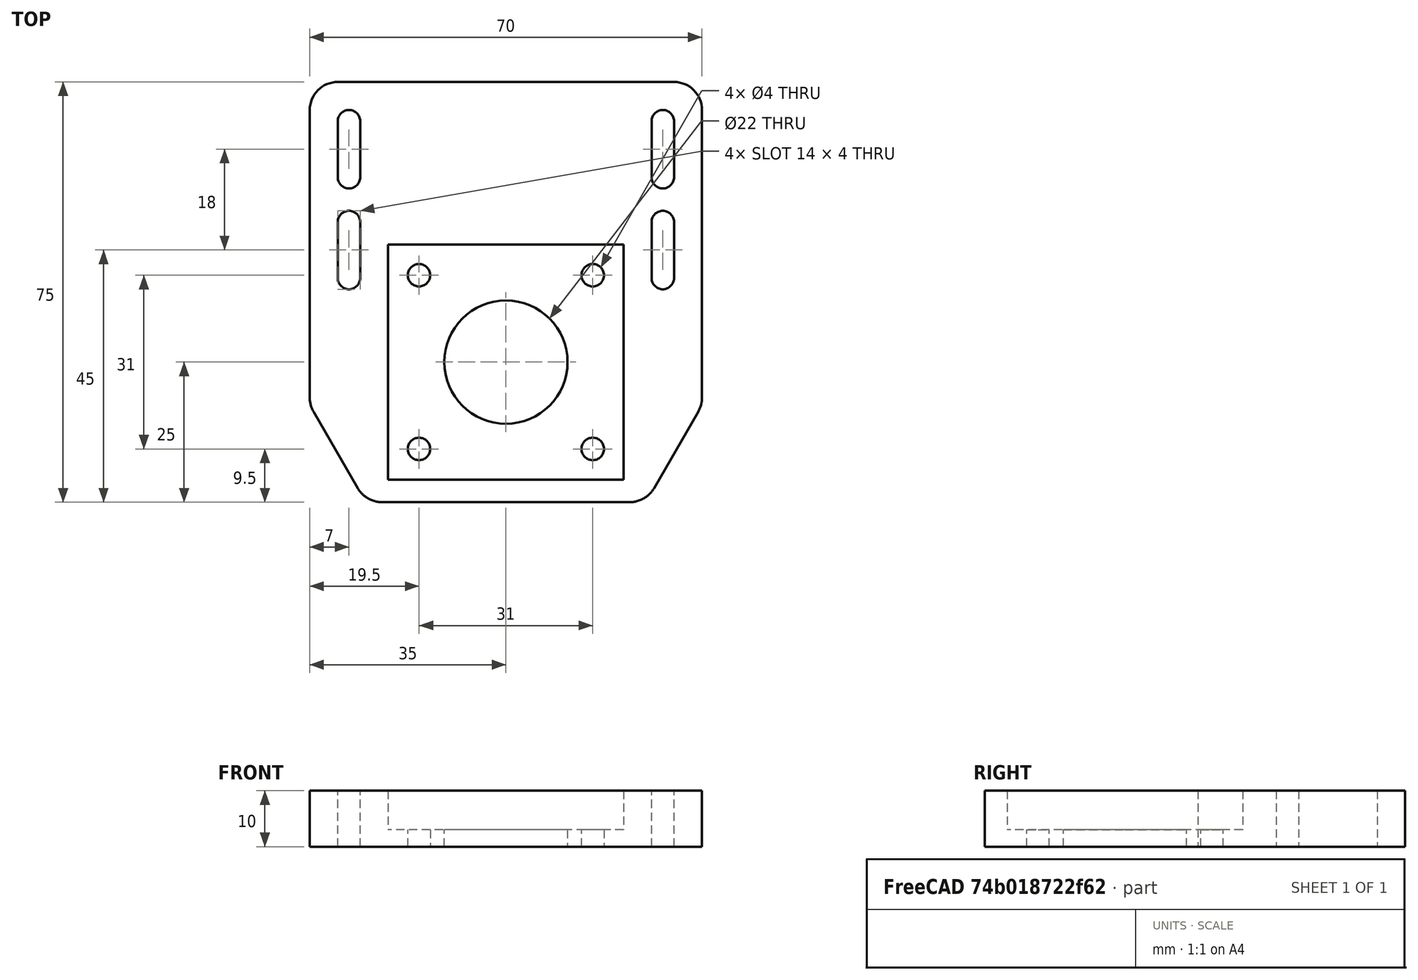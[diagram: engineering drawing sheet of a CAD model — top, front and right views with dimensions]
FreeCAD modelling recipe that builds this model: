
FCSTD DOCUMENT  (FreeCAD 2020.12.13R23076 +3015 (Git))
Label: krokowiec-dol
License: All rights reserved
objects: Sketcher::SketchObject×7, PartDesign::Pocket×4, PartDesign::Pad×2, PartDesign::LinearPattern×2, TechDraw::DrawProjGroupItem×2, TechDraw::DrawViewDimension×2, TechDraw::DrawSVGTemplate×1, PartDesign::MultiTransform×1, PartDesign::Fillet×1, PartDesign::Body×1, TechDraw::DrawProjGroup×1, TechDraw::DrawPage×1
note: 35 computed .brp shape members not serialized (recipe doc carries the construction recipe); baked Part::Feature solids carry a one-line shape summary decoded from their .brp

FEATURE [Sketcher::SketchObject] Sketch
  MapMode = 5
  Support = -> [XY_Plane]
  sketch-geometry (5):
    g0: LineSegment StartX=25 StartY=25 StartZ=0 EndX=-25 EndY=25 EndZ=0
    g1: LineSegment StartX=-25 StartY=-25 StartZ=0 EndX=25 EndY=-25 EndZ=0
    g2: Circle [constr] CenterX=0 CenterY=0 CenterZ=0 NormalX=0 NormalY=0 NormalZ=1 AngleXU=0 Radius=35.3553
    g3: LineSegment StartX=-25 StartY=25 StartZ=0 EndX=-25 EndY=-25 EndZ=0
    g4: LineSegment StartX=25 StartY=25 StartZ=0 EndX=25 EndY=-25 EndZ=0
  constraints (14):
    c: Equal(g0,g1)
    c: PointOnObject(g0,g2)
    c: PointOnObject(g1,g2)
    c: PointOnObject(g1,g2)
    c: PointOnObject(g0,g2)
    c: Coincident(g2,g-1)
    c: Horizontal(g0)
    c: DistanceX(g0,g0) = 50
    c: DistanceY(g1,g0) = 50
    c: Horizontal(g1)
    c: Coincident(g0,g3)
    c: Coincident(g3,g1)
    c: Coincident(g0,g4)
    c: Coincident(g4,g1)
FEATURE [PartDesign::Pad] Pad
  ClaimChildren = false
  Direction = (1,1,1)
  Fit = 0
  FitJoin = 0
  InnerFit = 0
  InnerFitJoin = 0
  InnerTaperAngle = 0
  InnerTaperAngleRev = 0
  Length = 10
  Length2 = 100
  NewSolid = false
  Profile = -> Sketch
  Suppress = false
  Type = 0
FEATURE [Sketcher::SketchObject] Sketch001
  MapMode = 5
  Placement = pos=(0,0,10) rot=(0,0,1;0rad)
  Support = -> [Pad]
  sketch-geometry (5):
    g0: LineSegment StartX=21 StartY=21 StartZ=0 EndX=-21 EndY=21 EndZ=0
    g1: LineSegment StartX=-21 StartY=21 StartZ=0 EndX=-21 EndY=-21 EndZ=0
    g2: LineSegment StartX=-21 StartY=-21 StartZ=0 EndX=21 EndY=-21 EndZ=0
    g3: LineSegment StartX=21 StartY=-21 StartZ=0 EndX=21 EndY=21 EndZ=0
    g4: Circle [constr] CenterX=0 CenterY=0 CenterZ=0 NormalX=0 NormalY=0 NormalZ=1 AngleXU=0 Radius=29.6985
  constraints (14):
    c: Coincident(g0,g1)
    c: Coincident(g1,g2)
    c: Coincident(g2,g3)
    c: Coincident(g3,g0)
    c: Equal(g0,g1)
    c: Equal(g0,g2)
    c: Equal(g0,g3)
    c: PointOnObject(g0,g4)
    c: PointOnObject(g1,g4)
    c: PointOnObject(g2,g4)
    c: PointOnObject(g3,g4)
    c: Coincident(g4,g-1)
    c: DistanceX(g0,g0) = 42
    c: Horizontal(g0)
FEATURE [PartDesign::Pocket] Pocket
  BaseFeature = -> Pad
  ClaimChildren = false
  Fit = 0
  FitJoin = 0
  InnerFit = 0
  InnerFitJoin = 0
  InnerTaperAngle = 0
  InnerTaperAngleRev = 0
  Length = 7
  Length2 = 100
  NewSolid = false
  Profile = -> Sketch001
  Suppress = false
  Type = 0
FEATURE [Sketcher::SketchObject] Sketch002
  MapMode = 5
  Placement = pos=(0,0,3) rot=(0,0,1;0rad)
  Support = -> [Pocket]
  sketch-geometry (1):
    g0: Circle CenterX=0 CenterY=0 CenterZ=0 NormalX=0 NormalY=0 NormalZ=1 AngleXU=0 Radius=11
  constraints (2):
    c: Coincident(g0,g-1)
    c: Diameter(g0) = 22
FEATURE [PartDesign::Pocket] Pocket001
  BaseFeature = -> Pocket
  ClaimChildren = false
  Fit = 0
  FitJoin = 0
  InnerFit = 0
  InnerFitJoin = 0
  InnerTaperAngle = 0
  InnerTaperAngleRev = 0
  Length = 5
  Length2 = 100
  NewSolid = false
  Profile = -> Sketch002
  Suppress = false
  Type = 1
FEATURE [Sketcher::SketchObject] Sketch005
  MapMode = 5
  Placement = pos=(0,0,5) rot=(0,0,1;0rad)
  sketch-geometry (4):
    g0: Circle CenterX=-15.5 CenterY=15.5 CenterZ=0 NormalX=0 NormalY=0 NormalZ=1 AngleXU=0 Radius=2
    g1: Circle CenterX=15.5 CenterY=15.5 CenterZ=0 NormalX=0 NormalY=0 NormalZ=1 AngleXU=0 Radius=2
    g2: Circle CenterX=15.5 CenterY=-15.5 CenterZ=0 NormalX=0 NormalY=0 NormalZ=1 AngleXU=0 Radius=2
    g3: Circle CenterX=-15.5 CenterY=-15.5 CenterZ=0 NormalX=0 NormalY=0 NormalZ=1 AngleXU=0 Radius=2
  constraints (9):
    c: Symmetric(g3,g0,g-1)
    c: Symmetric(g0,g1,g-2)
    c: Symmetric(g2,g1,g-1)
    c: Equal(g3,g2)
    c: Equal(g2,g1)
    c: Equal(g1,g0)
    c: DistanceX(g0,g1) = 31
    c: DistanceY(g2,g1) = 31
    c: Diameter(g1) = 4
FEATURE [PartDesign::Pocket] Pocket004
  BaseFeature = -> Pocket001
  ClaimChildren = false
  Fit = 0
  FitJoin = 0
  InnerFit = 0
  InnerFitJoin = 0
  InnerTaperAngle = 0
  InnerTaperAngleRev = 0
  Length = 5
  Length2 = 100
  NewSolid = false
  Profile = -> Sketch005
  Suppress = false
  Type = 0
FEATURE [Sketcher::SketchObject] Sketch007
  MapMode = 5
  Support = -> [XY_Plane]
  sketch-geometry (4):
    g0: ArcOfCircle CenterX=-28 CenterY=15 CenterZ=0 NormalX=0 NormalY=0 NormalZ=1 AngleXU=0 Radius=2 StartAngle=3.14159 EndAngle=6.28319
    g1: ArcOfCircle CenterX=-28 CenterY=25 CenterZ=0 NormalX=0 NormalY=0 NormalZ=1 AngleXU=0 Radius=2 StartAngle=0 EndAngle=3.14159
    g2: LineSegment StartX=-26 StartY=15 StartZ=0 EndX=-26 EndY=25 EndZ=0
    g3: LineSegment StartX=-30 StartY=15 StartZ=0 EndX=-30 EndY=25 EndZ=0
  constraints (10):
    c: Tangent(g0,g3) = 1.5708
    c: Tangent(g0,g2) = -1.5708
    c: Tangent(g2,g1) = -1.5708
    c: Tangent(g3,g1) = 1.5708
    c: Vertical(g2)
    c: Equal(g0,g1)
    c: Radius(g1) = 2
    c: DistanceY(g0,g1) = 10
    c: DistanceY(g0) = 15
    c: DistanceX(g0,g-1) = 28
FEATURE [PartDesign::LinearPattern] LinearPattern
  CopyShape = false
  Direction = -> Sketch007 [H_Axis]
  Length = 56
  NewSolid = false
  Occurrences = 2
  SubTransform = true
  Suppress = false
FEATURE [PartDesign::LinearPattern] LinearPattern001
  CopyShape = false
  Direction = -> Sketch007 [V_Axis]
  Length = 18
  NewSolid = false
  Occurrences = 2
  SubTransform = true
  Suppress = false
FEATURE [TechDraw::DrawSVGTemplate] Template
  EditableTexts = Designed_by_Name=Designed by Name; Drawing_number=Drawing number; FC-Date=Date; FC-SC=Scale; FC-SH=Sheet; FC-Title=Title; Subtitle=Subtitle; Weight=Weight
  Height = 210
  Orientation = 1
  Width = 297
FEATURE [Sketcher::SketchObject] Sketch006
  ExternalGeometry = -> [Pocket004]
  MapMode = 5
  Support = -> [XY_Plane]
  sketch-geometry (8):
    g0: LineSegment StartX=-25 StartY=25 StartZ=0 EndX=25 EndY=25 EndZ=0
    g1: LineSegment StartX=35 StartY=-7.67949 StartZ=0 EndX=35 EndY=50 EndZ=0
    g2: LineSegment StartX=35 StartY=50 StartZ=0 EndX=-35 EndY=50 EndZ=0
    g3: LineSegment StartX=-35 StartY=50 StartZ=0 EndX=-35 EndY=-7.67949 EndZ=0
    g4: LineSegment StartX=-35 StartY=-7.67949 StartZ=0 EndX=-25 EndY=-25 EndZ=0
    g5: LineSegment StartX=-25 StartY=-25 StartZ=0 EndX=-25 EndY=25 EndZ=0
    g6: LineSegment StartX=35 StartY=-7.67949 StartZ=0 EndX=25 EndY=-25 EndZ=0
    g7: LineSegment StartX=25 StartY=-25 StartZ=0 EndX=25 EndY=25 EndZ=0
  constraints (19):
    c: Coincident(g-3,g0)
    c: Coincident(g0,g-3)
    c: Vertical(g1)
    c: Coincident(g1,g2)
    c: Coincident(g2,g3)
    c: Symmetric(g2,g1,g-2)
    c: Symmetric(g3,g1,g-2)
    c: DistanceX(g2,g2) = 70
    c: DistanceY(g1) = 50
    c: Coincident(g3,g4)
    c: Coincident(g4,g5)
    c: Coincident(g5,g0)
    c: Vertical(g5)
    c: Coincident(g1,g6)
    c: Coincident(g6,g7)
    c: Coincident(g7,g0)
    c: Symmetric(g6,g4,g-2)
    c: Angle(g1,g6) = 2.61799
    c: DistanceY(g6) = -25
FEATURE [PartDesign::Pad] Pad001
  BaseFeature = -> Pocket004
  ClaimChildren = false
  Direction = (1,1,1)
  Fit = 0
  FitJoin = 0
  InnerFit = 0
  InnerFitJoin = 0
  InnerTaperAngle = 0
  InnerTaperAngleRev = 0
  Length = 10
  Length2 = 100
  NewSolid = false
  Profile = -> Sketch006
  Suppress = false
  Type = 0
FEATURE [PartDesign::Pocket] Pocket005
  BaseFeature = -> Pad001
  ClaimChildren = false
  Fit = 0
  FitJoin = 0
  InnerFit = 0
  InnerFitJoin = 0
  InnerTaperAngle = 0
  InnerTaperAngleRev = 0
  Length = 5
  Length2 = 100
  NewSolid = false
  Profile = -> Sketch007
  Reversed = true
  Suppress = false
  Type = 1
FEATURE [PartDesign::MultiTransform] MultiTransform
  BaseFeature = -> Pocket005
  CopyShape = false
  NewSolid = false
  OriginalSubs = -> [Pocket005]
  Originals = -> [Pocket005]
  SubTransform = true
  Suppress = false
  Transformations = -> [LinearPattern,LinearPattern001]
FEATURE [PartDesign::Fillet] Fillet
  Base = -> MultiTransform [Edge48,Edge45,Edge31,Edge32,Edge44,Edge50]
  BaseFeature = -> MultiTransform
  NewSolid = false
  Radius = 5
  SupportTransform = true
  Suppress = false
FEATURE [Sketcher::SketchObject] Sketch008
  ExternalGeometry = -> [Fillet]
  MapMode = 5
  Support = -> [XY_Plane]
  sketch-geometry (3):
    g0: GeomPoint X=-28 Y=43 Z=0
    g1: GeomPoint X=28 Y=43 Z=0
    g2: LineSegment StartX=-28 StartY=43 StartZ=0 EndX=28 EndY=43 EndZ=0
  constraints (4):
    c: Coincident(g0,g-3)
    c: Coincident(g1,g-4)
    c: Coincident(g2,g0)
    c: Coincident(g2,g1)
FEATURE [PartDesign::Body] Body  label="krokowiec-dol"
  ExportMode = 0
  Group = -> [Sketch,Pad,Sketch001,Pocket,Sketch002,Pocket001,Sketch005,Pocket004,Sketch006,Pad001,Sketch007,Pocket005,MultiTransform,LinearPattern,LinearPattern001,Fillet,Sketch008]
  Origin = -> Origin
  Tip = -> Fillet
  _ExportChildren = -> [Pad,Pocket,Pocket001,Pocket004,Pad001,Pocket005,MultiTransform,LinearPattern,LinearPattern001,Fillet,Sketch008]
  _GroupVersion = 1
FEATURE [TechDraw::DrawProjGroupItem] ProjItem  label="Front"
  CoarseView = false
  Direction = (0,0,1)
  Focus = 100
  HardHidden = false
  IsoCount = 0
  IsoHidden = false
  IsoVisible = false
  LockPosition = true
  Perspective = false
  Rotation = 0
  RotationVector = (1,0,0)
  ScaleType = 2
  SeamHidden = false
  SeamVisible = true
  SmoothHidden = false
  SmoothVisible = true
  Source = -> [Fillet]
  Type = 0
  X = 0
  XDirection = (1,0,0)
  Y = 0
FEATURE [TechDraw::DrawProjGroupItem] ProjItem001  label="Bottom"
  CoarseView = false
  Direction = (0,-1,0)
  Focus = 100
  HardHidden = false
  IsoCount = 0
  IsoHidden = false
  IsoVisible = false
  LockPosition = false
  Perspective = false
  Rotation = 0
  RotationVector = (1,0,0)
  ScaleType = 2
  SeamHidden = false
  SeamVisible = true
  SmoothHidden = false
  SmoothVisible = true
  Source = -> [Fillet]
  Type = 5
  X = 0
  XDirection = (1,0,0)
  Y = 57.5
FEATURE [TechDraw::DrawProjGroup] ProjGroup
  Anchor = -> ProjItem
  AutoDistribute = true
  LockPosition = false
  ProjectionType = 0
  Rotation = 0
  ScaleType = 0
  Source = -> [Fillet]
  Views = -> [ProjItem,ProjItem001]
  X = 148.5
  Y = 105
  spacingX = 15
  spacingY = 15
FEATURE [TechDraw::DrawViewDimension] Dimension
  Arbitrary = false
  FormatSpec = %.2f
  Inverted = false
  LockPosition = false
  MeasureType = 1
  OverTolerance = 0
  References2D = -> [ProjItem]
  Rotation = 0
  ScaleType = 0
  TheoreticalExact = false
  Type = 1
  UnderTolerance = 0
  X = 0
  Y = -18.25
FEATURE [TechDraw::DrawViewDimension] Dimension001
  Arbitrary = false
  FormatSpec = ⌀%.2f
  Inverted = false
  LockPosition = false
  MeasureType = 1
  OverTolerance = 0
  References2D = -> [ProjItem]
  Rotation = 0
  ScaleType = 0
  TheoreticalExact = false
  Type = 5
  UnderTolerance = 0
  X = 54.5294
  Y = 6.58114
FEATURE [TechDraw::DrawPage] Page
  KeepUpdated = true
  NextBalloonIndex = 1
  ProjectionType = 0
  Template = -> Template
  Views = -> [ProjGroup,Dimension,Dimension001]
